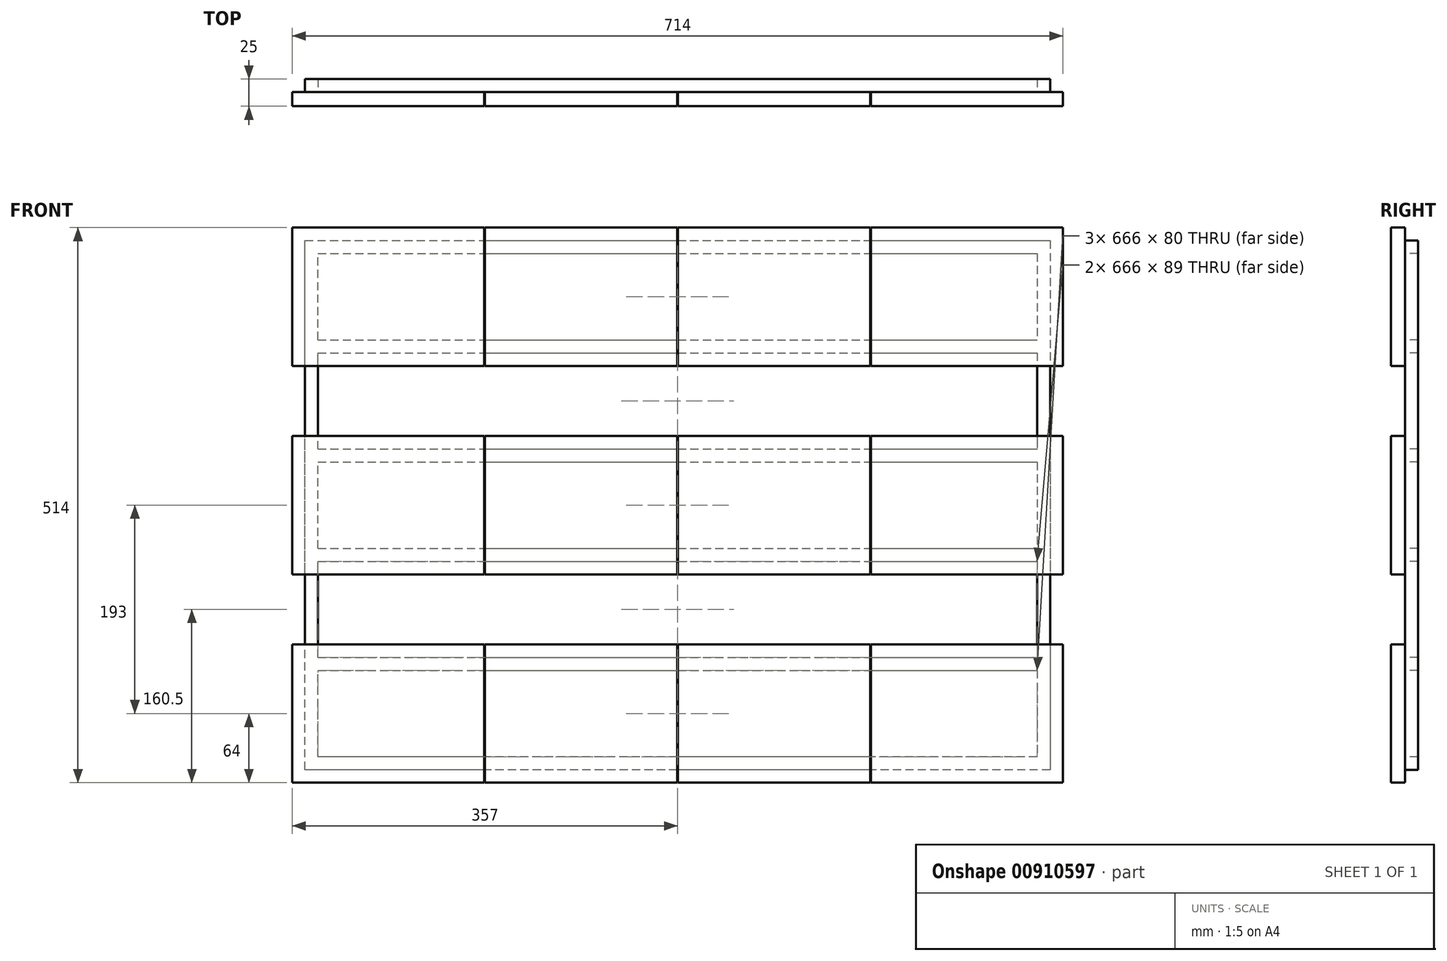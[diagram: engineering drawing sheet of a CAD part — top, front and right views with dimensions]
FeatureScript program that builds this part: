
annotation { "Feature Type Name" : "Feature", "Feature Type Description" : "" }
export const myFeature = defineFeature(function(context is Context, id is Id, definition is map)
    precondition{}
    {
        {
            var Q0;
            Q0=qCreatedBy(makeId("Front.planeOp"),FACE);
            var sketch = newSketch(context, id + "F0", { "sketchPlane" : qUnion([Q0])});
            skLineSegment(sketch, "E0", {"start": v(0, 0) * mm, "end": v(714, 0) * mm, "construction": true});
            skLineSegment(sketch, "E1", {"start": v(714, 0) * mm, "end": v(714, -514) * mm, "construction": true});
            skLineSegment(sketch, "E2", {"start": v(714, -514) * mm, "end": v(0, -514) * mm, "construction": true});
            skLineSegment(sketch, "E3", {"start": v(0, -514) * mm, "end": v(0, 0) * mm, "construction": true});
            skLineSegment(sketch, "E4.0", {"start": v(24, -24) * mm, "end": v(690, -24) * mm});
            skLineSegment(sketch, "E4.1", {"start": v(24, -490) * mm, "end": v(24, -410) * mm});
            skLineSegment(sketch, "E4.2", {"start": v(690, -490) * mm, "end": v(24, -490) * mm});
            skLineSegment(sketch, "E4.3", {"start": v(690, -24) * mm, "end": v(690, -104) * mm});
            skLineSegment(sketch, "E5", {"start": v(24, -116) * mm, "end": v(690, -116) * mm});
            skLineSegment(sketch, "E6", {"start": v(24, -205) * mm, "end": v(690, -205) * mm});
            skLineSegment(sketch, "E7", {"start": v(24, -309) * mm, "end": v(690, -309) * mm});
            skLineSegment(sketch, "E8", {"start": v(24, -398) * mm, "end": v(690, -398) * mm});
            skLineSegment(sketch, "E9.0", {"start": v(24, -104) * mm, "end": v(690, -104) * mm});
            skLineSegment(sketch, "E10.0", {"start": v(24, -217) * mm, "end": v(690, -217) * mm});
            skLineSegment(sketch, "E11.0", {"start": v(24, -410) * mm, "end": v(690, -410) * mm});
            skLineSegment(sketch, "E12.0", {"start": v(24, -297) * mm, "end": v(690, -297) * mm});
            skLineSegment(sketch, "E13.trimOffspring", {"start": v(690, -116) * mm, "end": v(690, -205) * mm});
            skLineSegment(sketch, "E14.trimOffspring", {"start": v(690, -217) * mm, "end": v(690, -297) * mm});
            skLineSegment(sketch, "E15.trimOffspring", {"start": v(690, -309) * mm, "end": v(690, -398) * mm});
            skLineSegment(sketch, "E16.trimOffspring", {"start": v(690, -410) * mm, "end": v(690, -490) * mm});
            skLineSegment(sketch, "E17.trimOffspring", {"start": v(24, -104) * mm, "end": v(24, -24) * mm});
            skLineSegment(sketch, "E18.trimOffspring", {"start": v(24, -205) * mm, "end": v(24, -116) * mm});
            skLineSegment(sketch, "E19.trimOffspring", {"start": v(24, -398) * mm, "end": v(24, -309) * mm});
            skLineSegment(sketch, "E20.trimOffspring", {"start": v(24, -297) * mm, "end": v(24, -217) * mm});
            skLineSegment(sketch, "E21.0", {"start": v(12, -502) * mm, "end": v(12, -12) * mm});
            skLineSegment(sketch, "E21.1", {"start": v(702, -502) * mm, "end": v(12, -502) * mm});
            skLineSegment(sketch, "E21.2", {"start": v(702, -12) * mm, "end": v(702, -502) * mm});
            skLineSegment(sketch, "E21.3", {"start": v(12, -12) * mm, "end": v(702, -12) * mm});
            skSolve(sketch);
        }
        {
            var Q0;
            Q0=makeQuery(id+"F0.imprint","IMPRINT",FACE,{"disambiguationData":[TD([[makeQuery(id+"F0.imprint","IMPRINT",EDGE,{"derivedFrom":sQuery(id+"F0.wireOp",EDGE,"E4.0")}),1.0]])]});
            extrude(context, id + "F1", {"entities" : qUnion([Q0]), "oppositeDirection" : true, "depth" : 12 * mm, "offsetDistance" : 25 * mm});
        }
        {
            var Q0;
            Q0=qCreatedBy(makeId("Front.planeOp"),FACE);
            var sketch = newSketch(context, id + "F2", { "sketchPlane" : qUnion([Q0])});
            skLineSegment(sketch, "E22.bottom", {"start": v(0, 0) * mm, "end": v(178, 0) * mm});
            skLineSegment(sketch, "E22.top", {"start": v(0, -128) * mm, "end": v(178, -128) * mm});
            skLineSegment(sketch, "E22.left", {"start": v(0, 0) * mm, "end": v(0, -128) * mm});
            skLineSegment(sketch, "E22.right", {"start": v(178, 0) * mm, "end": v(178, -128) * mm});
            skLineSegment(sketch, "E23.bottom", {"start": v(178.67, 0) * mm, "end": v(356.67, 0) * mm});
            skLineSegment(sketch, "E23.top", {"start": v(178.67, -128) * mm, "end": v(356.67, -128) * mm});
            skLineSegment(sketch, "E23.left", {"start": v(178.67, 0) * mm, "end": v(178.67, -128) * mm});
            skLineSegment(sketch, "E23.right", {"start": v(356.67, 0) * mm, "end": v(356.67, -128) * mm});
            skLineSegment(sketch, "E24.bottom", {"start": v(357.33, 0) * mm, "end": v(535.33, 0) * mm});
            skLineSegment(sketch, "E24.top", {"start": v(357.33, -128) * mm, "end": v(535.33, -128) * mm});
            skLineSegment(sketch, "E24.left", {"start": v(357.33, 0) * mm, "end": v(357.33, -128) * mm});
            skLineSegment(sketch, "E24.right", {"start": v(535.33, 0) * mm, "end": v(535.33, -128) * mm});
            skLineSegment(sketch, "E25.bottom", {"start": v(536, 0) * mm, "end": v(714, 0) * mm});
            skLineSegment(sketch, "E25.top", {"start": v(536, -128) * mm, "end": v(714, -128) * mm});
            skLineSegment(sketch, "E25.left", {"start": v(536, 0) * mm, "end": v(536, -128) * mm});
            skLineSegment(sketch, "E25.right", {"start": v(714, 0) * mm, "end": v(714, -128) * mm});
            skLineSegment(sketch, "E26.bottom", {"start": v(0, -193) * mm, "end": v(178, -193) * mm});
            skLineSegment(sketch, "E26.top", {"start": v(0, -321) * mm, "end": v(178, -321) * mm});
            skLineSegment(sketch, "E26.left", {"start": v(0, -193) * mm, "end": v(0, -321) * mm});
            skLineSegment(sketch, "E26.right", {"start": v(178, -193) * mm, "end": v(178, -321) * mm});
            skLineSegment(sketch, "E27.bottom", {"start": v(178.67, -193) * mm, "end": v(356.67, -193) * mm});
            skLineSegment(sketch, "E27.top", {"start": v(178.67, -321) * mm, "end": v(356.67, -321) * mm});
            skLineSegment(sketch, "E27.left", {"start": v(178.67, -193) * mm, "end": v(178.67, -321) * mm});
            skLineSegment(sketch, "E27.right", {"start": v(356.67, -193) * mm, "end": v(356.67, -321) * mm});
            skLineSegment(sketch, "E28.bottom", {"start": v(357.33, -193) * mm, "end": v(535.33, -193) * mm});
            skLineSegment(sketch, "E28.top", {"start": v(357.33, -321) * mm, "end": v(535.33, -321) * mm});
            skLineSegment(sketch, "E28.left", {"start": v(357.33, -193) * mm, "end": v(357.33, -321) * mm});
            skLineSegment(sketch, "E28.right", {"start": v(535.33, -193) * mm, "end": v(535.33, -321) * mm});
            skLineSegment(sketch, "E29.bottom", {"start": v(536, -193) * mm, "end": v(714, -193) * mm});
            skLineSegment(sketch, "E29.top", {"start": v(536, -321) * mm, "end": v(714, -321) * mm});
            skLineSegment(sketch, "E29.left", {"start": v(536, -193) * mm, "end": v(536, -321) * mm});
            skLineSegment(sketch, "E29.right", {"start": v(714, -193) * mm, "end": v(714, -321) * mm});
            skLineSegment(sketch, "E30.bottom", {"start": v(0, -386) * mm, "end": v(178, -386) * mm});
            skLineSegment(sketch, "E30.top", {"start": v(0, -514) * mm, "end": v(178, -514) * mm});
            skLineSegment(sketch, "E30.left", {"start": v(0, -386) * mm, "end": v(0, -514) * mm});
            skLineSegment(sketch, "E30.right", {"start": v(178, -386) * mm, "end": v(178, -514) * mm});
            skLineSegment(sketch, "E31.bottom", {"start": v(178.67, -386) * mm, "end": v(356.67, -386) * mm});
            skLineSegment(sketch, "E31.top", {"start": v(178.67, -514) * mm, "end": v(356.67, -514) * mm});
            skLineSegment(sketch, "E31.left", {"start": v(178.67, -386) * mm, "end": v(178.67, -514) * mm});
            skLineSegment(sketch, "E31.right", {"start": v(356.67, -386) * mm, "end": v(356.67, -514) * mm});
            skLineSegment(sketch, "E32.bottom", {"start": v(357.33, -386) * mm, "end": v(535.33, -386) * mm});
            skLineSegment(sketch, "E32.top", {"start": v(357.33, -514) * mm, "end": v(535.33, -514) * mm});
            skLineSegment(sketch, "E32.left", {"start": v(357.33, -386) * mm, "end": v(357.33, -514) * mm});
            skLineSegment(sketch, "E32.right", {"start": v(535.33, -386) * mm, "end": v(535.33, -514) * mm});
            skLineSegment(sketch, "E33.bottom", {"start": v(536, -386) * mm, "end": v(714, -386) * mm});
            skLineSegment(sketch, "E33.top", {"start": v(536, -514) * mm, "end": v(714, -514) * mm});
            skLineSegment(sketch, "E33.left", {"start": v(536, -386) * mm, "end": v(536, -514) * mm});
            skLineSegment(sketch, "E33.right", {"start": v(714, -386) * mm, "end": v(714, -514) * mm});
            skLineSegment(sketch, "E34", {"start": v(178, 0) * mm, "end": v(178.67, 0) * mm, "construction": true});
            skLineSegment(sketch, "E35", {"start": v(356.67, 0) * mm, "end": v(357.33, 0) * mm, "construction": true});
            skLineSegment(sketch, "E36", {"start": v(535.33, 0) * mm, "end": v(536, 0) * mm, "construction": true});
            skLineSegment(sketch, "E37", {"start": v(0, -128) * mm, "end": v(0, -193) * mm, "construction": true});
            skLineSegment(sketch, "E38", {"start": v(0, -321) * mm, "end": v(0, -386) * mm, "construction": true});
            skSolve(sketch);
        }
        {
            var Q0;
            Q0=qSketchRegion(id+"F2",true);
            extrude(context, id + "F3", {"entities" : qUnion([Q0]), "depth" : 13 * mm, "offsetDistance" : 25 * mm});
        }
    });
